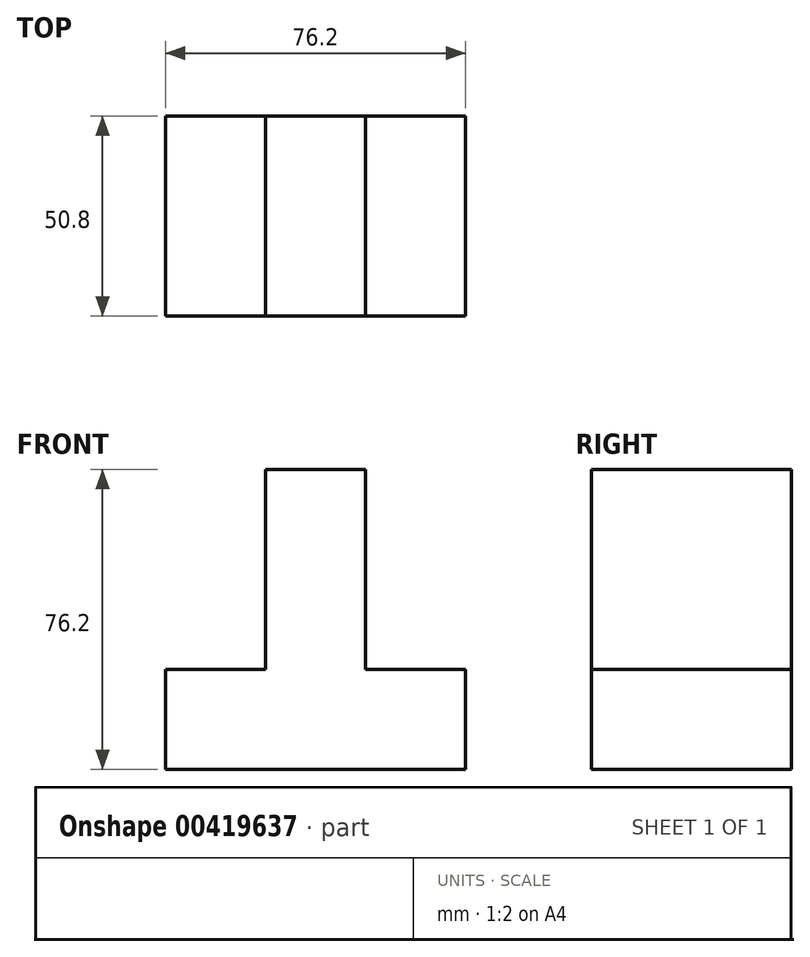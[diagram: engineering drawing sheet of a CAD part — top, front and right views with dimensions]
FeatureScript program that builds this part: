
annotation { "Feature Type Name" : "Feature", "Feature Type Description" : "" }
export const myFeature = defineFeature(function(context is Context, id is Id, definition is map)
    precondition{}
    {
        {
            var Q0;
            Q0=qCreatedBy(makeId("Front.planeOp"),FACE);
            var sketch = newSketch(context, id + "F0", { "sketchPlane" : qUnion([Q0])});
            skLineSegment(sketch, "E0", {"start": v(0, 0) * mm, "end": v(76.2, 0) * mm});
            skLineSegment(sketch, "E1", {"start": v(0, 0) * mm, "end": v(0, 25.4) * mm});
            skLineSegment(sketch, "E2", {"start": v(0, 25.4) * mm, "end": v(25.4, 25.4) * mm});
            skLineSegment(sketch, "E3", {"start": v(25.4, 25.4) * mm, "end": v(25.4, 76.2) * mm});
            skLineSegment(sketch, "E4", {"start": v(76.2, 0) * mm, "end": v(76.2, 25.4) * mm});
            skLineSegment(sketch, "E5", {"start": v(76.2, 25.4) * mm, "end": v(50.8, 25.4) * mm});
            skLineSegment(sketch, "E6", {"start": v(50.8, 25.4) * mm, "end": v(50.8, 76.2) * mm});
            skLineSegment(sketch, "E7", {"start": v(25.4, 76.2) * mm, "end": v(50.8, 76.2) * mm});
            skSolve(sketch);
        }
        {
            var Q0;
            Q0 = qSketchRegion(id + "F0", true);
            extrude(context, id + "F1", {"entities" : qUnion([Q0]), "depth" : 50.8 * mm});
        }
    });
